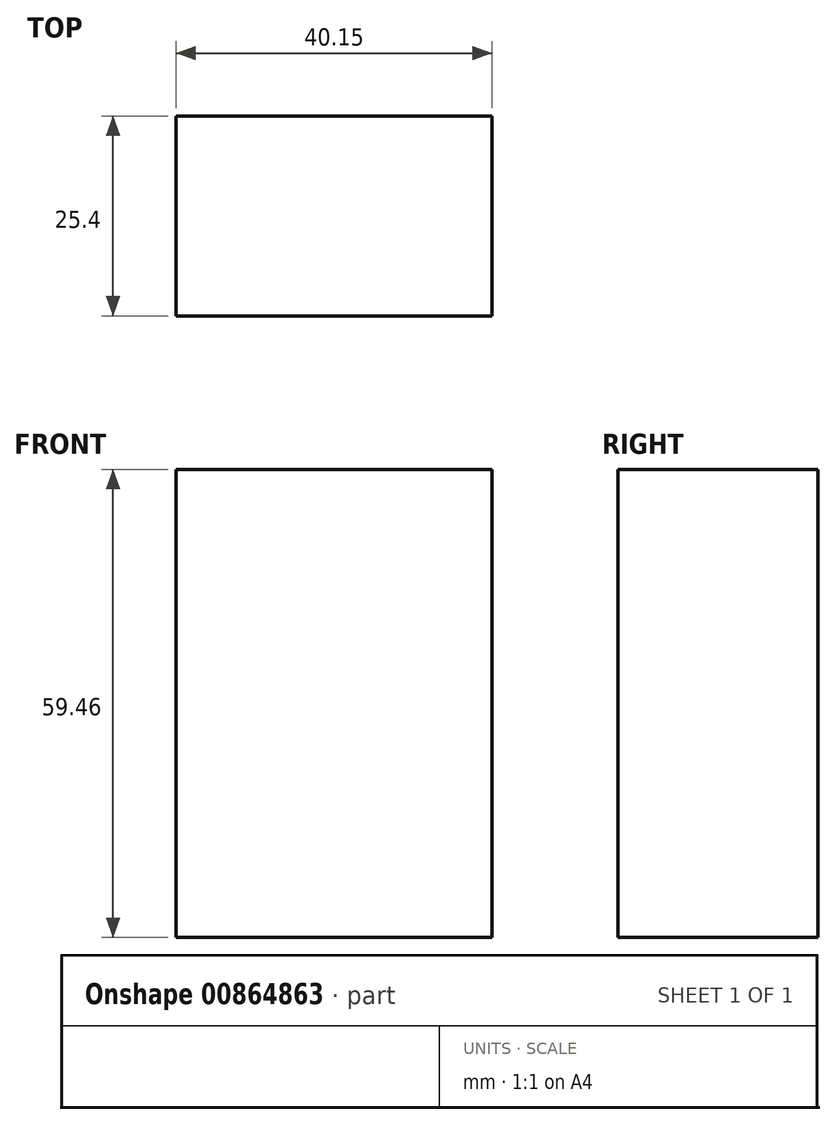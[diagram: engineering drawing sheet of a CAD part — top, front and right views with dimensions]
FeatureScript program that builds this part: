
annotation { "Feature Type Name" : "Feature", "Feature Type Description" : "" }
export const myFeature = defineFeature(function(context is Context, id is Id, definition is map)
    precondition{}
    {
        {
            var Q0;
            Q0=qCreatedBy(makeId("Front.planeOp"),FACE);
            var sketch = newSketch(context, id + "F0", { "sketchPlane" : qUnion([Q0])});
            skLineSegment(sketch, "E0.bottom", {"start": v(-62.6, 41.52) * mm, "end": v(-22.45, 41.52) * mm});
            skLineSegment(sketch, "E0.top", {"start": v(-62.6, -17.94) * mm, "end": v(-22.45, -17.94) * mm});
            skLineSegment(sketch, "E0.left", {"start": v(-62.6, 41.52) * mm, "end": v(-62.6, -17.94) * mm});
            skLineSegment(sketch, "E0.right", {"start": v(-22.45, 41.52) * mm, "end": v(-22.45, -17.94) * mm});
            skSolve(sketch);
        }
        {
            var Q0;
            Q0=makeQuery(id+"F0.imprint","IMPRINT",FACE,{"disambiguationData":[TD([[makeQuery(id+"F0.imprint","IMPRINT",EDGE,{"derivedFrom":sQuery(id+"F0.wireOp",EDGE,"E0.bottom")}),-1.0]])]});
            extrude(context, id + "F1", {"entities" : qUnion([Q0]), "depth" : 25.4 * mm, "offsetDistance" : 25.4 * mm});
        }
    });
